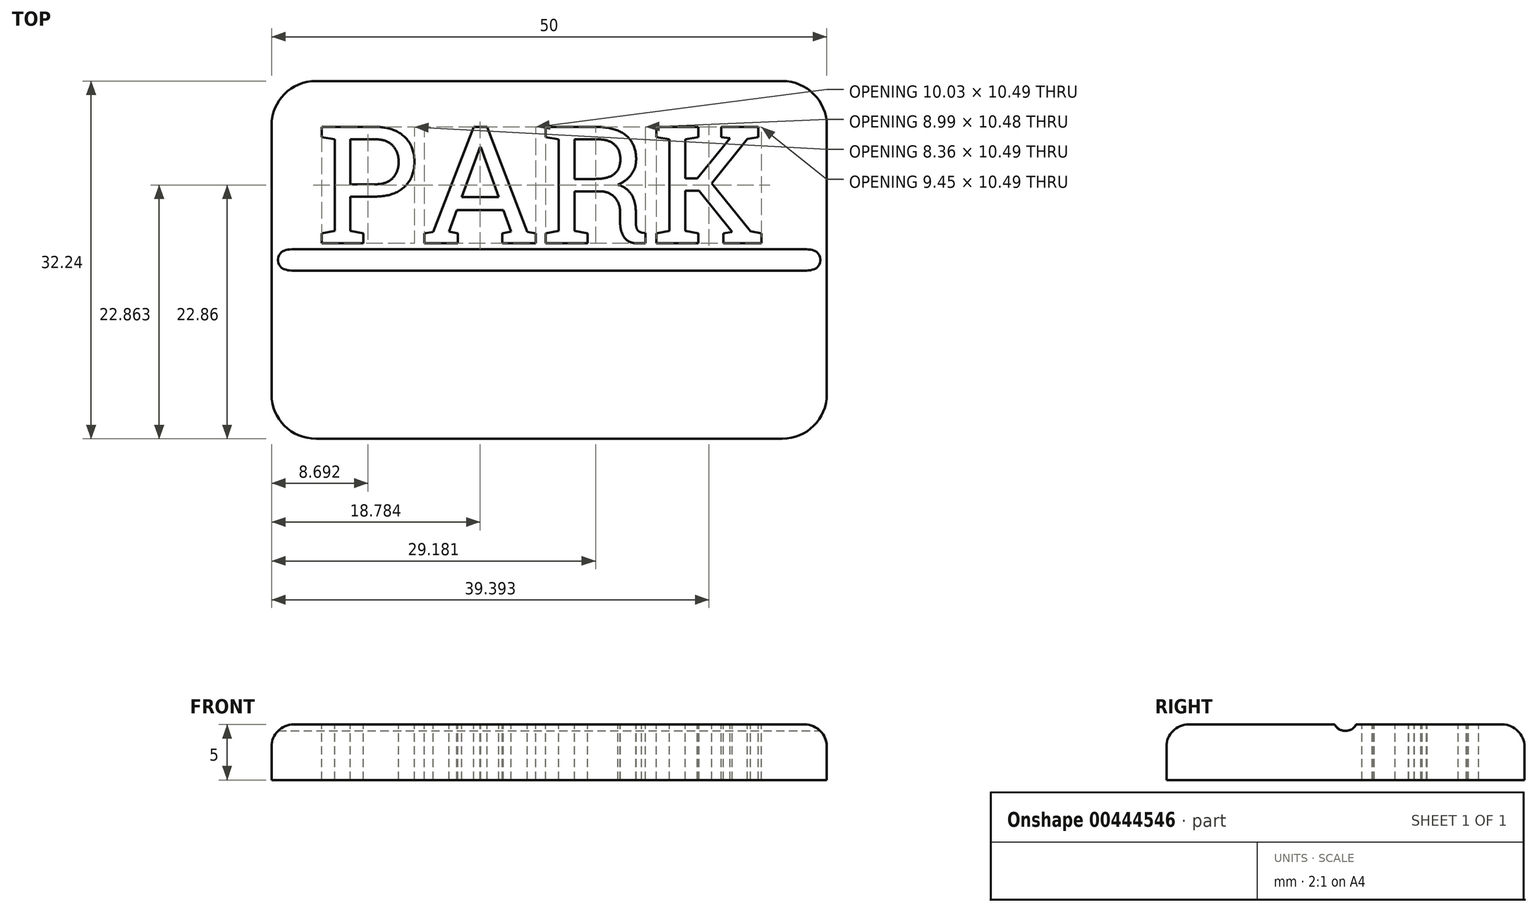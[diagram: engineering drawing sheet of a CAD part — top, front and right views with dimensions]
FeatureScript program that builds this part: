
annotation { "Feature Type Name" : "Feature", "Feature Type Description" : "" }
export const myFeature = defineFeature(function(context is Context, id is Id, definition is map)
    precondition{}
    {
        {
            var Q0;
            Q0=qCreatedBy(makeId("Top.planeOp"),FACE);
            var sketch = newSketch(context, id + "F0", { "sketchPlane" : qUnion([Q0])});
            skLineSegment(sketch, "E0.bottom", {"start": v(21, 16.12) * mm, "end": v(-21, 16.12) * mm});
            skLineSegment(sketch, "E0.top", {"start": v(21, -16.12) * mm, "end": v(-21, -16.12) * mm});
            skLineSegment(sketch, "E0.left", {"start": v(25, 12.12) * mm, "end": v(25, -12.12) * mm});
            skLineSegment(sketch, "E0.right", {"start": v(-25, 12.12) * mm, "end": v(-25, -12.12) * mm});
            skPoint(sketch, "E0.middle", {"position": v(0, 0) * mm});
            skPoint(sketch, "E1.visualSharp", {"position": v(-25, 16.12) * mm});
            skArc(sketch, "E1.filletArc", {"start": v(-21, 16.12) * mm, "mid": v(-23.83, 14.95) * mm, "end": v(-25, 12.12) * mm});
            skPoint(sketch, "E2.visualSharp", {"position": v(25, 16.12) * mm});
            skArc(sketch, "E2.filletArc", {"start": v(25, 12.12) * mm, "mid": v(23.83, 14.95) * mm, "end": v(21, 16.12) * mm});
            skPoint(sketch, "E3.visualSharp", {"position": v(25, -16.12) * mm});
            skArc(sketch, "E3.filletArc", {"start": v(21, -16.12) * mm, "mid": v(23.83, -14.95) * mm, "end": v(25, -12.12) * mm});
            skPoint(sketch, "E4.visualSharp", {"position": v(-25, -16.12) * mm});
            skArc(sketch, "E4.filletArc", {"start": v(-25, -12.12) * mm, "mid": v(-23.83, -14.95) * mm, "end": v(-21, -16.12) * mm});
            skSolve(sketch);
        }
        {
            var Q0;
            Q0=makeQuery(id+"F0.imprint","IMPRINT",FACE,{"disambiguationData":[TD([[makeQuery(id+"F0.imprint","IMPRINT",EDGE,{"derivedFrom":sQuery(id+"F0.wireOp",EDGE,"E0.bottom")}),1.0]])]});
            extrude(context, id + "F1", {"entities" : qUnion([Q0]), "depth" : 5 * mm});
        }
        {
            var Q0;
            Q0=makeQuery(id+"F1.opExtrude","CAP_FACE",FACE,{"disambiguationData":[OSD([sQuery(id+"F0.wireOp",EDGE,"E0.bottom"),sQuery(id+"F0.wireOp",EDGE,"E0.top"),sQuery(id+"F0.wireOp",EDGE,"E0.left"),sQuery(id+"F0.wireOp",EDGE,"E0.right"),sQuery(id+"F0.wireOp",EDGE,"E1.filletArc"),sQuery(id+"F0.wireOp",EDGE,"E2.filletArc"),sQuery(id+"F0.wireOp",EDGE,"E3.filletArc"),sQuery(id+"F0.wireOp",EDGE,"E4.filletArc")])],"isStart":false});
            var sketch = newSketch(context, id + "F2", { "sketchPlane" : qUnion([Q0])});
            skText(sketch, "E5", { "text": "PARK", "fontName": "RobotoSlab-Regular.ttf"});
            skPoint(sketch, "E6.middle", {"position": v(0, -9.16) * mm});
            const initialGuessF2  = {"E5": [-0.021, 0.0015, 1, 0, 0.01062]};
            skSetInitialGuess(sketch, initialGuessF2);
            skSolve(sketch);
        }
        {
            var Q0;
            Q0 = qSketchRegion(id + "F2", true);
            extrude(context, id + "F3", {"entities" : qUnion([Q0]), "operationType" : NewBodyOperationType.REMOVE, "oppositeDirection" : true, "depth" : 5 * mm});
        }
        {
            var Q0;
            Q0=makeQuery(id+"F1.opExtrude","CAP_EDGE",EDGE,{"disambiguationData":[OSD([sQuery(id+"F0.wireOp",EDGE,"E0.bottom")])],"isStart":false});
            var Q1;
            Q1=makeQuery(id+"F1.opExtrude","CAP_EDGE",EDGE,{"disambiguationData":[OSD([sQuery(id+"F0.wireOp",EDGE,"E1.filletArc")])],"isStart":false});
            var Q2;
            Q2=makeQuery(id+"F1.opExtrude","CAP_EDGE",EDGE,{"disambiguationData":[OSD([sQuery(id+"F0.wireOp",EDGE,"E0.right")])],"isStart":false});
            fillet(context, id + "F4", {"entities" : qUnion([Q0, Q1, Q2]), "radius" : 2 * mm, "tangentPropagation" : true, "allowEdgeOverflow" : false});
        }
        {
            var Q0;
            Q0=qCreatedBy(makeId("Right.planeOp"),FACE);
            var sketch = newSketch(context, id + "F5", { "sketchPlane" : qUnion([Q0])});
            skCircle(sketch, "E7", {"center": v(0, 5.51) * mm, "radius": 1.1 * mm});
            skSolve(sketch);
        }
        {
            var Q0;
            Q0 = qSketchRegion(id + "F5", true);
            var Q1;
            Q1=sQuery(id+"F5.wireOp",EDGE,"E7");
            extrude(context, id + "F6", {"entities" : qUnion([Q0]), "operationType" : NewBodyOperationType.REMOVE, "surfaceEntities" : qUnion([Q1]), "endBound" : BoundingType.SYMMETRIC, "oppositeDirection" : true, "depth" : 50 * mm});
        }
    });
